# Revit family: Nuaire_IfcFanType_S2e
name_source: partatom
category: Mechanical Equipment
revit_build: Autodesk Revit 2018 (Build: 20170223_1515(x64)
units: mm (PartAtom-declared; Revit-internal decimal feet)

## family parameters
Always vertical = Yes
Cut with Voids When Loaded = No
OmniClass Number = 23.75.00.00
OmniClass Title = Climate Control (HVAC)
Part Type = Normal
Room Calculation Point = No
Round Connector Dimension = Use Diameter
Shared = No
Work Plane-Based = No

## types (4) — shared parameters
6 Monthly = e.g. SFG20 03-02
Annually = e.g. SFG20 03-02
BMS Links = Yes
Battery Supply = No
CE Approval = Yes
COBie.Type = Yes
COBie.Type.Category = Centrifugal Fans
COBie.Type.Description = Inline Centrifugal Extract Fan
COBie.Type.DurationUnit = Years
COBie.Type.Manufacturer = Nuaire
COBie.Type.WarrantyDescription = 2 years. First year parts and labour, remianing year parts only.
COBie.Type.WarrantyDurationLabor = 1
COBie.Type.WarrantyDurationParts = 2
COBie.Type.WarrantyDurationUnit = Year
COBie.Type.WarrantyGuarantorLabor = Nuaire
COBie.Type.WarrantyGuarantorParts = Nuaire
Catalogue Pages = https://www.nuaire.co.uk
Classification.Uniclass.Pr.Description = Centrifugal Fans
Classification.Uniclass.Pr.Number = Pr_65_67_29_12
Daily = e.g. SFG20 03-02
Description = Inline Centrifugal Extract Fan
Enclosure Rating = Not IP rated
Environmental Product Declaration = WEEE, RoHS
Fax Number = +44(0)2920-858-222
Features = Lined top and bottom panel, EC backward curved blower, Class L2 Leakage, onboard controls for trickle/boost/purge, circular spigots, hanging brackets
Fire Control Panel Links = No
Frequency = 50 Hz
Full Load Current = 1 A
I&M Manual = http://nuaire.info
IFCExportAs = IfcFanType
IFCExportType = CENTRIFUGALBACKWARDINCLINEDCURVED
Location of Manufacturer = 51.571856, -3.232638
Maintenance Required 0 to 300hrs = http://nuaire.info
Maintenance Required 1001 to 2000hrs = http://nuaire.info
Maintenance Required 2001 to 4000hrs = http://nuaire.info
Maintenance Required 301 to 600hrs = http://nuaire.info
Maintenance Required 4001 to 8000hrs = http://nuaire.info
Maintenance Required 601 to 1000hrs = http://nuaire.info
Maintenance Required 8001 to 12000hrs = http://nuaire.info
Manufacturer = Nuaire
Manufacturer Website = http://www.nuaire.co.uk
Maximum Ambient Temperature = 40 °C
Monthly = e.g. SFG20 03-02
Number of Connection Poles = 2
Number of Motor Poles = 2
OmniClass Number = 23-33 31 19 13
OmniClass Title = Centrifugal Fans
Operation and Maintenance Manual = http://nuaire.info
Postcode = CF83 1NA
Power Source = Mains
Product Literature = https://www.nuaire.co.uk
Product Range = S2E
Quarterly = e.g. SFG20 03-02
Reference Standard = ISO 9001:2015
Responsible Sourcing of Materials = FSC
Revit Family Last Revised = 2021-01-14T11:22:00
Starting Current = 1 A
Supply Phase = 1
Telephone Number = +44(0)2920-858-200
URL = http://www.nuaire.co.uk
VAT Registration Number = 877308
Voltage = 230 V
Weatherproof or Internal Only = Internal
Weekly = e.g. SFG20 03-02
bracket_length = 105 mm
zero-valued in all types: COBie.Type.Area, COBie.Type.ReplacementCost, Cost, Life Cycle Analysis

## per-type parameters (varying)
| type | Access Clearance Bottom | Apparent Load | COBie.Type.NominalHeight | COBie.Type.NominalLength | COBie.Type.NominalWidth | Height | Length | Nominal Motor Rating | Nominal Motor Speed (rpm) | Spigot Diameter | Weight | Width | overall_bracket_length | power_offset_left | power_offset_top | spigot_ID | spigot_length | spigot_offset_height | spigot_offset_left |
| S2E-125 | 186 mm  [stored 0.610236 ft] | 173 VA | 186 mm  [stored 0.610236 ft] | 475 mm  [stored 1.5584 ft] | 299 mm  [stored 0.980971 ft] | 186 mm  [stored 0.610236 ft] | 475 mm  [stored 1.5584 ft] | 0.083 kW | 3200 | 125 mm  [stored 0.410105 ft] | 7.40 kg | 299 mm  [stored 0.980971 ft] | 543 mm  [stored 1.7815 ft] | 24 mm | 19 mm | 121 mm  [stored 0.396982 ft] | 44 mm  [stored 0.144357 ft] | 93 mm  [stored 0.305118 ft] | 165 mm |
| S2E-150 | 186 mm  [stored 0.610236 ft] | 207 VA | 186 mm  [stored 0.610236 ft] | 475 mm  [stored 1.5584 ft] | 299 mm  [stored 0.980971 ft] | 186 mm  [stored 0.610236 ft] | 475 mm  [stored 1.5584 ft] | 0.115 kW | 3635 | 150 mm | 7.40 kg | 299 mm  [stored 0.980971 ft] | 543 mm  [stored 1.7815 ft] | 24 mm | 19 mm | 146 mm  [stored 0.479003 ft] | 44 mm  [stored 0.144357 ft] | 93 mm  [stored 0.305118 ft] | 165 mm |
| S2E-200 | 234 mm  [stored 0.767717 ft] | 311 VA | 234 mm  [stored 0.767717 ft] | 577 mm  [stored 1.89304 ft] | 339 mm  [stored 1.1122 ft] | 234 mm  [stored 0.767717 ft] | 577 mm  [stored 1.89304 ft] | 0.169 kW | 4120 | 200 mm  [stored 0.656168 ft] | 9.80 kg | 339 mm  [stored 1.1122 ft] | 648 mm  [stored 2.12598 ft] | 24 mm | 32 mm | 196 mm  [stored 0.643045 ft] | 45 mm | 117 mm  [stored 0.383858 ft] | 190 mm |
| S2E-250 | 288 mm  [stored 0.944882 ft] | 322 VA | 288 mm  [stored 0.944882 ft] | 677 mm  [stored 2.22113 ft] | 409 mm  [stored 1.34186 ft] | 288 mm  [stored 0.944882 ft] | 677 mm  [stored 2.22113 ft] | 0.170 kW | 2519 | 250 mm  [stored 0.82021 ft] | 13.20 kg | 409 mm  [stored 1.34186 ft] | 750 mm  [stored 2.46063 ft] | 25 mm  [stored 0.082021 ft] | 32 mm | 246 mm  [stored 0.807087 ft] | 47 mm | 144 mm  [stored 0.472441 ft] | 220 mm |

note: column(s) folded — value = type name in every type: COBie.Type.ModelNumber, COBie.Type.ModelReference, COBie.Type.Name, Model

note: [stored X ft] marks values corroborated as IEEE doubles in the binary element streams (Revit-internal decimal feet)

## geometry (parser evidence)
native form markers: Sweep x2
no freeform markers — native parametric forms only
